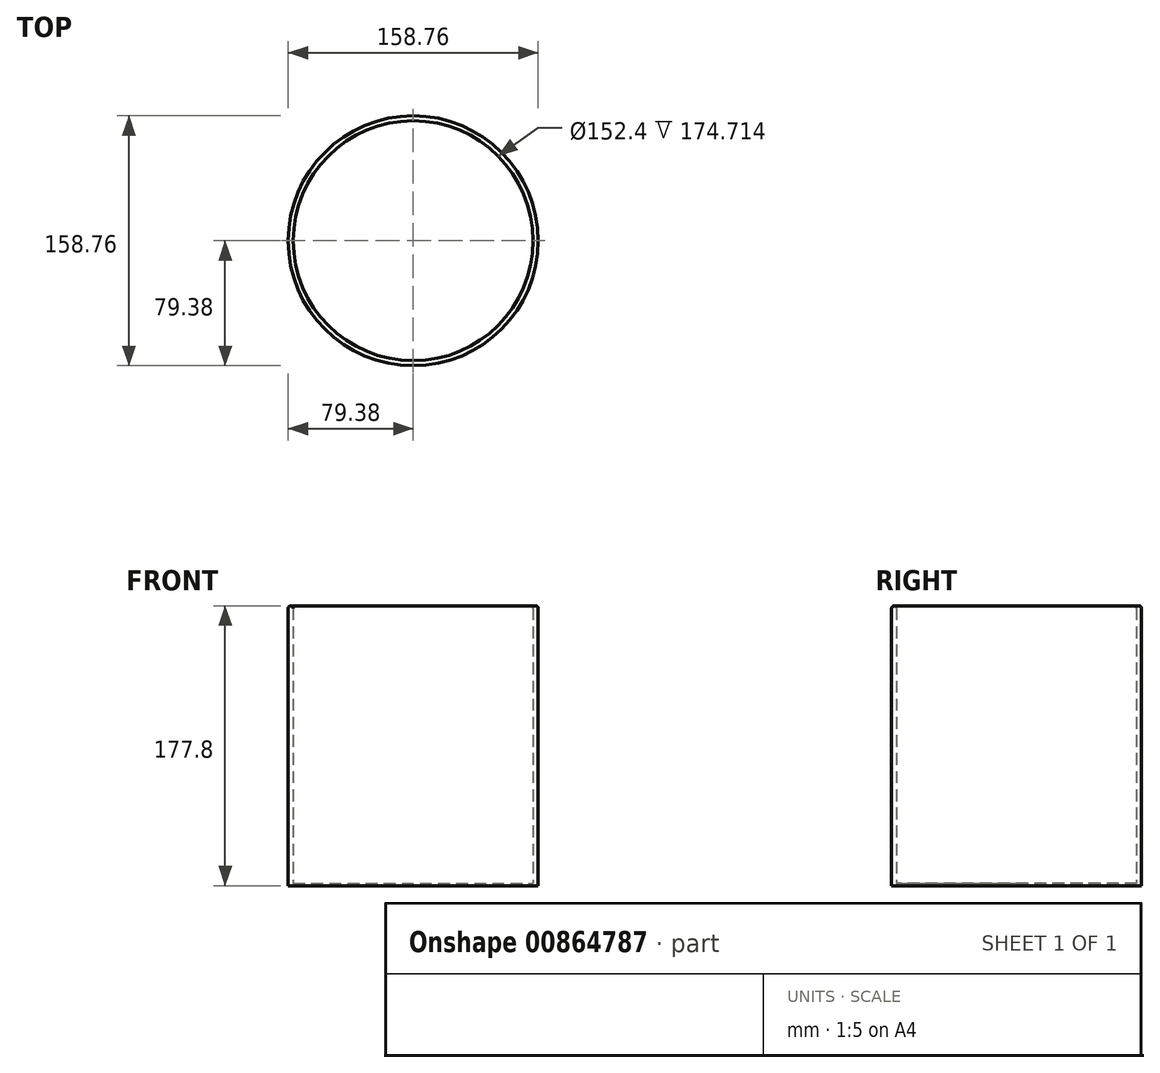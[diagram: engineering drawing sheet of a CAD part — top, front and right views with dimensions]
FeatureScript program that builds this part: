
annotation { "Feature Type Name" : "Feature", "Feature Type Description" : "" }
export const myFeature = defineFeature(function(context is Context, id is Id, definition is map)
    precondition{}
    {
        {
            var Q0;
            Q0=qCreatedBy(makeId("Front.planeOp"),FACE);
            var sketch = newSketch(context, id + "F0", { "sketchPlane" : qUnion([Q0])});
            skLineSegment(sketch, "E0", {"start": v(0, 0) * mm, "end": v(0, 1.5) * mm});
            skLineSegment(sketch, "E1", {"start": v(0, 1.5) * mm, "end": v(-76.2, 1.5) * mm});
            skLineSegment(sketch, "E2", {"start": v(0, 0) * mm, "end": v(-79.38, 0) * mm});
            skLineSegment(sketch, "E3", {"start": v(-79.38, 0) * mm, "end": v(-79.38, 177.8) * mm});
            skLineSegment(sketch, "E4", {"start": v(-76.2, 177.8) * mm, "end": v(-76.2, 1.5) * mm});
            skArc(sketch, "E5", {"start": v(-76.2, 176.21) * mm, "mid": v(-77.79, 177.8) * mm, "end": v(-79.38, 176.21) * mm});
            skLineSegment(sketch, "E6", {"start": v(0, 1.5) * mm, "end": v(0, 77.7) * mm});
            skSolve(sketch);
        }
        {
            var Q0;
            Q0=makeQuery(id+"F0.imprint","IMPRINT",FACE,{"disambiguationData":[TD([[makeQuery(id+"F0.imprint","IMPRINT",EDGE,{"derivedFrom":sQuery(id+"F0.wireOp",EDGE,"E0")}),1.0]])]});
            var Q1;
            Q1=sQuery(id+"F0.wireOp",EDGE,"E6");
            revolve(context, id + "F1", {"surfaceOperationType" : NewSurfaceOperationType.NEW, "entities" : qUnion([Q0]), "axis" : qUnion([Q1]), "revolveType" : RevolveType.FULL});
        }
    });
